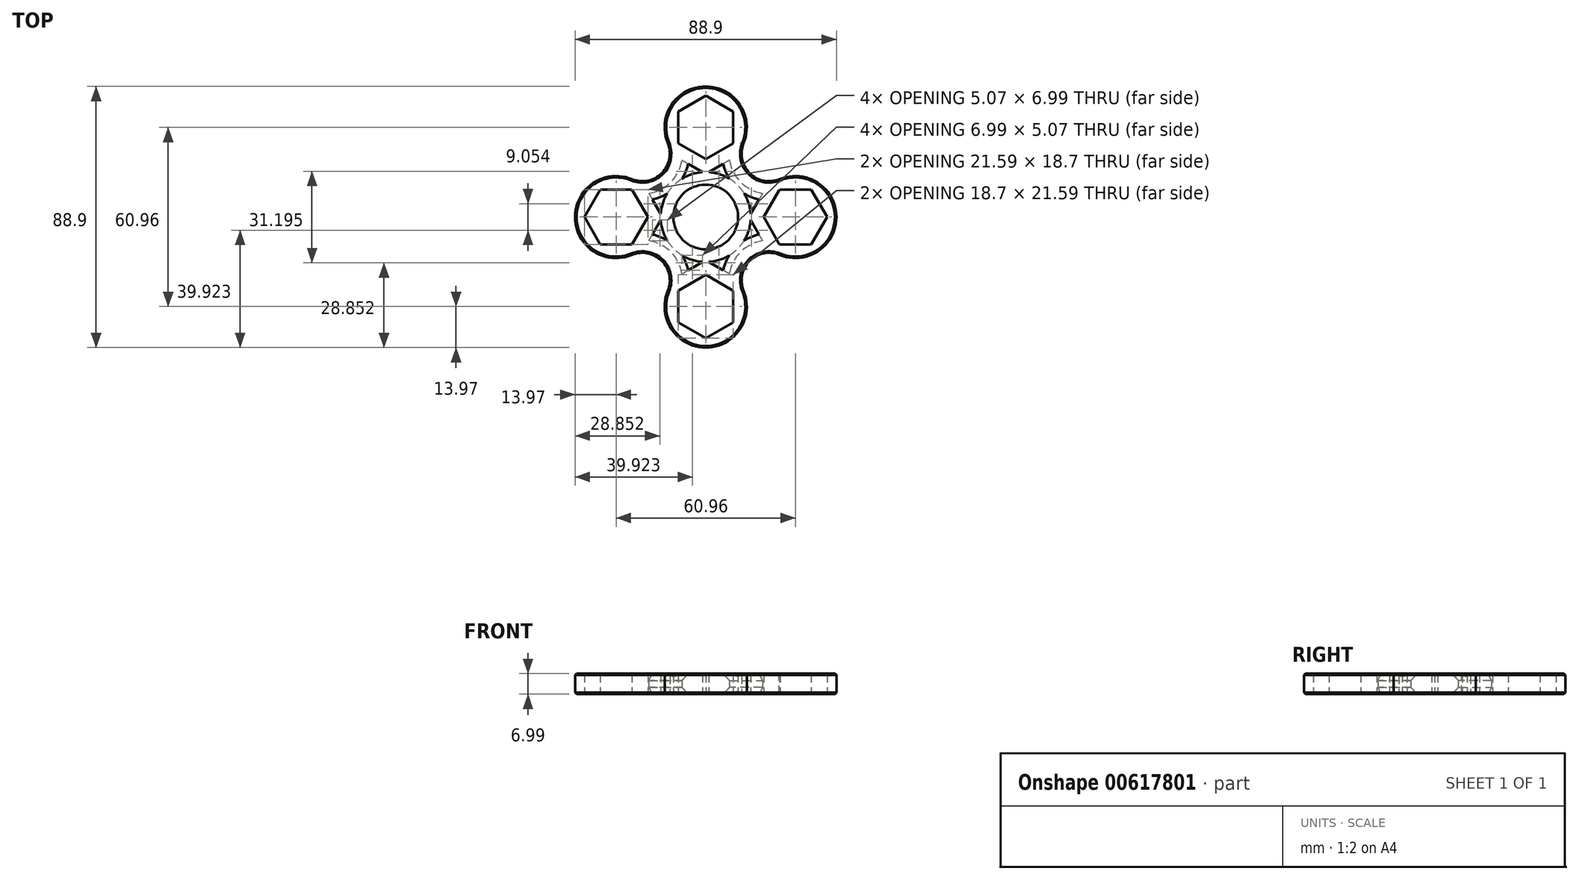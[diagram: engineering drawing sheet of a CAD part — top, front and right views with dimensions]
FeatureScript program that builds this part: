
annotation { "Feature Type Name" : "Feature", "Feature Type Description" : "" }
export const myFeature = defineFeature(function(context is Context, id is Id, definition is map)
    precondition{}
    {
        {
            var Q0;
            Q0=qCreatedBy(makeId("Top.planeOp"),FACE);
            var sketch = newSketch(context, id + "F0", { "sketchPlane" : qUnion([Q0])});
            skCircle(sketch, "E0", {"center": v(0, 0) * mm, "radius": 11.01 * mm});
            skLineSegment(sketch, "E1", {"start": v(0, 0) * mm, "end": v(0, -30.48) * mm});
            skLineSegment(sketch, "E2", {"start": v(0, 0) * mm, "end": v(30.48, 0) * mm});
            skLineSegment(sketch, "E3", {"start": v(0, 0) * mm, "end": v(-30.48, 0) * mm});
            skLineSegment(sketch, "E4", {"start": v(0, 0) * mm, "end": v(0, 30.48) * mm});
            skCircle(sketch, "E5.cCircle", {"center": v(-30.48, 0) * mm, "radius": 10.8 * mm, "construction": true});
            skLineSegment(sketch, "E5.0", {"start": v(-19.69, 0) * mm, "end": v(-25.08, -9.35) * mm});
            skLineSegment(sketch, "E5.1", {"start": v(-25.08, -9.35) * mm, "end": v(-35.88, -9.35) * mm});
            skLineSegment(sketch, "E5.2", {"start": v(-35.88, -9.35) * mm, "end": v(-41.27, 0) * mm});
            skLineSegment(sketch, "E5.3", {"start": v(-41.28, 0) * mm, "end": v(-35.88, 9.35) * mm});
            skLineSegment(sketch, "E5.4", {"start": v(-35.88, 9.35) * mm, "end": v(-25.08, 9.35) * mm});
            skLineSegment(sketch, "E5.5", {"start": v(-25.08, 9.35) * mm, "end": v(-19.69, 0) * mm});
            skCircle(sketch, "E6.cCircle", {"center": v(0, 30.48) * mm, "radius": 10.8 * mm, "construction": true});
            skLineSegment(sketch, "E6.0", {"start": v(9.35, 25.08) * mm, "end": v(0, 19.69) * mm});
            skLineSegment(sketch, "E6.1", {"start": v(0, 19.69) * mm, "end": v(-9.35, 25.08) * mm});
            skLineSegment(sketch, "E6.2", {"start": v(-9.35, 25.08) * mm, "end": v(-9.35, 35.88) * mm});
            skLineSegment(sketch, "E6.3", {"start": v(-9.35, 35.88) * mm, "end": v(0, 41.28) * mm});
            skLineSegment(sketch, "E6.4", {"start": v(0, 41.27) * mm, "end": v(9.35, 35.88) * mm});
            skLineSegment(sketch, "E6.5", {"start": v(9.35, 35.88) * mm, "end": v(9.35, 25.08) * mm});
            skCircle(sketch, "E7.cCircle", {"center": v(0, -30.48) * mm, "radius": 10.8 * mm, "construction": true});
            skLineSegment(sketch, "E7.0", {"start": v(9.35, -35.88) * mm, "end": v(0, -41.28) * mm});
            skLineSegment(sketch, "E7.1", {"start": v(0, -41.28) * mm, "end": v(-9.35, -35.88) * mm});
            skLineSegment(sketch, "E7.2", {"start": v(-9.35, -35.88) * mm, "end": v(-9.35, -25.08) * mm});
            skLineSegment(sketch, "E7.3", {"start": v(-9.35, -25.08) * mm, "end": v(0, -19.68) * mm});
            skLineSegment(sketch, "E7.4", {"start": v(0, -19.68) * mm, "end": v(9.35, -25.08) * mm});
            skLineSegment(sketch, "E7.5", {"start": v(9.35, -25.08) * mm, "end": v(9.35, -35.88) * mm});
            skCircle(sketch, "E8.cCircle", {"center": v(30.48, 0) * mm, "radius": 10.8 * mm, "construction": true});
            skLineSegment(sketch, "E8.0", {"start": v(35.88, 9.35) * mm, "end": v(41.28, 0) * mm});
            skLineSegment(sketch, "E8.1", {"start": v(41.27, 0) * mm, "end": v(35.88, -9.35) * mm});
            skLineSegment(sketch, "E8.2", {"start": v(35.88, -9.35) * mm, "end": v(25.08, -9.35) * mm});
            skLineSegment(sketch, "E8.3", {"start": v(25.08, -9.35) * mm, "end": v(19.68, 0) * mm});
            skLineSegment(sketch, "E8.4", {"start": v(19.68, 0) * mm, "end": v(25.08, 9.35) * mm});
            skLineSegment(sketch, "E8.5", {"start": v(25.08, 9.35) * mm, "end": v(35.88, 9.35) * mm});
            skCircle(sketch, "E9", {"center": v(-30.48, 0) * mm, "radius": 13.97 * mm});
            skCircle(sketch, "E10", {"center": v(0, 30.48) * mm, "radius": 13.97 * mm});
            skCircle(sketch, "E11", {"center": v(30.48, 0) * mm, "radius": 13.97 * mm});
            skCircle(sketch, "E12", {"center": v(0, -30.48) * mm, "radius": 13.97 * mm});
            skArc(sketch, "E13", {"start": v(-25.08, 12.89) * mm, "mid": v(-14.92, 14.95) * mm, "end": v(-12.9, 25.13) * mm});
            skArc(sketch, "E14", {"start": v(12.9, 25.13) * mm, "mid": v(14.92, 14.95) * mm, "end": v(25.08, 12.89) * mm});
            skArc(sketch, "E15", {"start": v(25.08, -12.89) * mm, "mid": v(14.92, -14.95) * mm, "end": v(12.9, -25.13) * mm});
            skLineSegment(sketch, "E16", {"start": v(-21.55, 21.55) * mm, "end": v(0, 0) * mm});
            skLineSegment(sketch, "E17", {"start": v(0, 0) * mm, "end": v(21.55, 21.55) * mm});
            skLineSegment(sketch, "E18", {"start": v(0, 0) * mm, "end": v(21.55, -21.55) * mm});
            skLineSegment(sketch, "E19", {"start": v(0, 0) * mm, "end": v(-21.55, -21.55) * mm});
            skArc(sketch, "E20", {"start": v(-25.13, -12.9) * mm, "mid": v(-14.95, -14.92) * mm, "end": v(-12.89, -25.08) * mm});
            skSolve(sketch);
        }
        {
            var Q0;
            Q0 = qSketchRegion(id + "F0", true);
            extrude(context, id + "F1", {"entities" : qUnion([Q0]), "depth" : 7 * mm, "offsetDistance" : 25.4 * mm});
        }
        {
            var Q0;
            Q0=makeQuery(id+"F1.opExtrude","CAP_EDGE",EDGE,{"disambiguationData":[OSD([sQuery(id+"F0.wireOp",EDGE,"E13")])],"isStart":true});
            var Q1;
            Q1=makeQuery(id+"F1.opExtrude","CAP_EDGE",EDGE,{"disambiguationData":[OSD([sQuery(id+"F0.wireOp",EDGE,"E14")])],"isStart":true});
            var Q2;
            Q2=makeQuery(id+"F1.opExtrude","CAP_EDGE",EDGE,{"disambiguationData":[OSD([sQuery(id+"F0.wireOp",EDGE,"E15")])],"isStart":true});
            var Q3;
            Q3=makeQuery(id+"F1.opExtrude","CAP_EDGE",EDGE,{"disambiguationData":[OSD([sQuery(id+"F0.wireOp",EDGE,"7jBfzRG3-1LJ6-chb8-GvcL-bCyCi3K84gJS")])],"isStart":true});
            var Q4;
            Q4=makeQuery(id+"F1.opExtrude","CAP_EDGE",EDGE,{"disambiguationData":[OSD([sQuery(id+"F0.wireOp",EDGE,"E10")])],"isStart":true});
            var Q5;
            Q5=makeQuery(id+"F1.opExtrude","CAP_EDGE",EDGE,{"disambiguationData":[OSD([sQuery(id+"F0.wireOp",EDGE,"E9")])],"isStart":true});
            var Q6;
            Q6=makeQuery(id+"F1.opExtrude","CAP_EDGE",EDGE,{"disambiguationData":[OSD([sQuery(id+"F0.wireOp",EDGE,"E12")])],"isStart":true});
            var Q7;
            Q7=makeQuery(id+"F1.opExtrude","CAP_EDGE",EDGE,{"disambiguationData":[OSD([sQuery(id+"F0.wireOp",EDGE,"E11")])],"isStart":true});
            chamfer(context, id + "F2", {"entities" : qUnion([Q0, Q1, Q2, Q3, Q4, Q5, Q6, Q7]), "width" : 0.5 * mm, "tangentPropagation" : true});
        }
        {
            var Q0;
            Q0=makeQuery(id+"F1.opExtrude","CAP_EDGE",EDGE,{"disambiguationData":[OSD([sQuery(id+"F0.wireOp",EDGE,"E9")])],"isStart":false});
            var Q1;
            Q1=makeQuery(id+"F1.opExtrude","CAP_EDGE",EDGE,{"disambiguationData":[OSD([sQuery(id+"F0.wireOp",EDGE,"E13")])],"isStart":false});
            var Q2;
            Q2=makeQuery(id+"F1.opExtrude","CAP_EDGE",EDGE,{"disambiguationData":[OSD([sQuery(id+"F0.wireOp",EDGE,"E10")])],"isStart":false});
            var Q3;
            Q3=makeQuery(id+"F1.opExtrude","SWEPT_EDGE",EDGE,{"disambiguationData":[OSD([sQuery(id+"F0.wireOp",EDGE,"E8.4"),sQuery(id+"F0.wireOp",EDGE,"E8.5")])]});
            var Q4;
            Q4=makeQuery(id+"F2.opChamfer","BLEND_EDGE",EDGE,{"blendedFrom":[makeQuery(id+"F1.opExtrude","CAP_EDGE",EDGE,{"disambiguationData":[OSD([sQuery(id+"F0.wireOp",EDGE,"E11")])],"isStart":true}),makeQuery(id+"F1.opExtrude","CAP_EDGE",EDGE,{"disambiguationData":[OSD([sQuery(id+"F0.wireOp",EDGE,"E14")])],"isStart":true})],"blendedInto":[]});
            var Q5;
            Q5=makeQuery(id+"F1.opExtrude","SWEPT_EDGE",EDGE,{"disambiguationData":[OSD([sQuery(id+"F0.wireOp",EDGE,"E11"),sQuery(id+"F0.wireOp",EDGE,"E14")])]});
            var Q6;
            Q6=makeQuery(id+"F1.opExtrude","CAP_EDGE",EDGE,{"disambiguationData":[OSD([sQuery(id+"F0.wireOp",EDGE,"E14")])],"isStart":false});
            var Q7;
            Q7=makeQuery(id+"F1.opExtrude","CAP_EDGE",EDGE,{"disambiguationData":[OSD([sQuery(id+"F0.wireOp",EDGE,"E11")])],"isStart":false});
            var Q8;
            Q8=makeQuery(id+"F1.opExtrude","CAP_EDGE",EDGE,{"disambiguationData":[OSD([sQuery(id+"F0.wireOp",EDGE,"E15")])],"isStart":false});
            var Q9;
            Q9=makeQuery(id+"F1.opExtrude","CAP_EDGE",EDGE,{"disambiguationData":[OSD([sQuery(id+"F0.wireOp",EDGE,"E12")])],"isStart":false});
            var Q10;
            Q10=makeQuery(id+"F1.opExtrude","CAP_EDGE",EDGE,{"disambiguationData":[OSD([sQuery(id+"F0.wireOp",EDGE,"7jBfzRG3-1LJ6-chb8-GvcL-bCyCi3K84gJS")])],"isStart":false});
            chamfer(context, id + "F3", {"entities" : qUnion([Q0, Q1, Q2, Q3, Q4, Q5, Q6, Q7, Q8, Q9, Q10]), "width" : 0.5 * mm, "tangentPropagation" : true});
        }
        {
            var Q0;
            Q0=makeQuery(id+"F1.opExtrude","CAP_FACE",FACE,{"disambiguationData":[OSD([sQuery(id+"F0.wireOp",EDGE,"E0"),sQuery(id+"F0.wireOp",EDGE,"E5.0"),sQuery(id+"F0.wireOp",EDGE,"E5.1"),sQuery(id+"F0.wireOp",EDGE,"E5.2"),sQuery(id+"F0.wireOp",EDGE,"E5.3"),sQuery(id+"F0.wireOp",EDGE,"E5.4"),sQuery(id+"F0.wireOp",EDGE,"E5.5"),sQuery(id+"F0.wireOp",EDGE,"E6.0"),sQuery(id+"F0.wireOp",EDGE,"E6.1"),sQuery(id+"F0.wireOp",EDGE,"E6.2"),sQuery(id+"F0.wireOp",EDGE,"E6.3"),sQuery(id+"F0.wireOp",EDGE,"E6.4"),sQuery(id+"F0.wireOp",EDGE,"E6.5"),sQuery(id+"F0.wireOp",EDGE,"E7.0"),sQuery(id+"F0.wireOp",EDGE,"E7.1"),sQuery(id+"F0.wireOp",EDGE,"E7.2"),sQuery(id+"F0.wireOp",EDGE,"E7.3"),sQuery(id+"F0.wireOp",EDGE,"E7.4"),sQuery(id+"F0.wireOp",EDGE,"E7.5"),sQuery(id+"F0.wireOp",EDGE,"E8.0"),sQuery(id+"F0.wireOp",EDGE,"E8.1"),sQuery(id+"F0.wireOp",EDGE,"E8.2"),sQuery(id+"F0.wireOp",EDGE,"E8.3"),sQuery(id+"F0.wireOp",EDGE,"E8.4"),sQuery(id+"F0.wireOp",EDGE,"E8.5"),sQuery(id+"F0.wireOp",EDGE,"E9"),sQuery(id+"F0.wireOp",EDGE,"E10"),sQuery(id+"F0.wireOp",EDGE,"E11"),sQuery(id+"F0.wireOp",EDGE,"E12"),sQuery(id+"F0.wireOp",EDGE,"E13"),sQuery(id+"F0.wireOp",EDGE,"E14"),sQuery(id+"F0.wireOp",EDGE,"E15"),sQuery(id+"F0.wireOp",EDGE,"7jBfzRG3-1LJ6-chb8-GvcL-bCyCi3K84gJS")])],"isStart":true});
            var Q1;
            Q1=makeQuery(id+"F1.opExtrude","CAP_FACE",FACE,{"disambiguationData":[OSD([sQuery(id+"F0.wireOp",EDGE,"E0"),sQuery(id+"F0.wireOp",EDGE,"E5.0"),sQuery(id+"F0.wireOp",EDGE,"E5.1"),sQuery(id+"F0.wireOp",EDGE,"E5.2"),sQuery(id+"F0.wireOp",EDGE,"E5.3"),sQuery(id+"F0.wireOp",EDGE,"E5.4"),sQuery(id+"F0.wireOp",EDGE,"E5.5"),sQuery(id+"F0.wireOp",EDGE,"E6.0"),sQuery(id+"F0.wireOp",EDGE,"E6.1"),sQuery(id+"F0.wireOp",EDGE,"E6.2"),sQuery(id+"F0.wireOp",EDGE,"E6.3"),sQuery(id+"F0.wireOp",EDGE,"E6.4"),sQuery(id+"F0.wireOp",EDGE,"E6.5"),sQuery(id+"F0.wireOp",EDGE,"E7.0"),sQuery(id+"F0.wireOp",EDGE,"E7.1"),sQuery(id+"F0.wireOp",EDGE,"E7.2"),sQuery(id+"F0.wireOp",EDGE,"E7.3"),sQuery(id+"F0.wireOp",EDGE,"E7.4"),sQuery(id+"F0.wireOp",EDGE,"E7.5"),sQuery(id+"F0.wireOp",EDGE,"E8.0"),sQuery(id+"F0.wireOp",EDGE,"E8.1"),sQuery(id+"F0.wireOp",EDGE,"E8.2"),sQuery(id+"F0.wireOp",EDGE,"E8.3"),sQuery(id+"F0.wireOp",EDGE,"E8.4"),sQuery(id+"F0.wireOp",EDGE,"E8.5"),sQuery(id+"F0.wireOp",EDGE,"E9"),sQuery(id+"F0.wireOp",EDGE,"E10"),sQuery(id+"F0.wireOp",EDGE,"E11"),sQuery(id+"F0.wireOp",EDGE,"E12"),sQuery(id+"F0.wireOp",EDGE,"E13"),sQuery(id+"F0.wireOp",EDGE,"E14"),sQuery(id+"F0.wireOp",EDGE,"E15"),sQuery(id+"F0.wireOp",EDGE,"7jBfzRG3-1LJ6-chb8-GvcL-bCyCi3K84gJS")])],"isStart":false});
            shell(context, id + "F4", {"entities" : qUnion([Q0, Q1]), "thickness" : 4.32 * mm});
        }
    });
